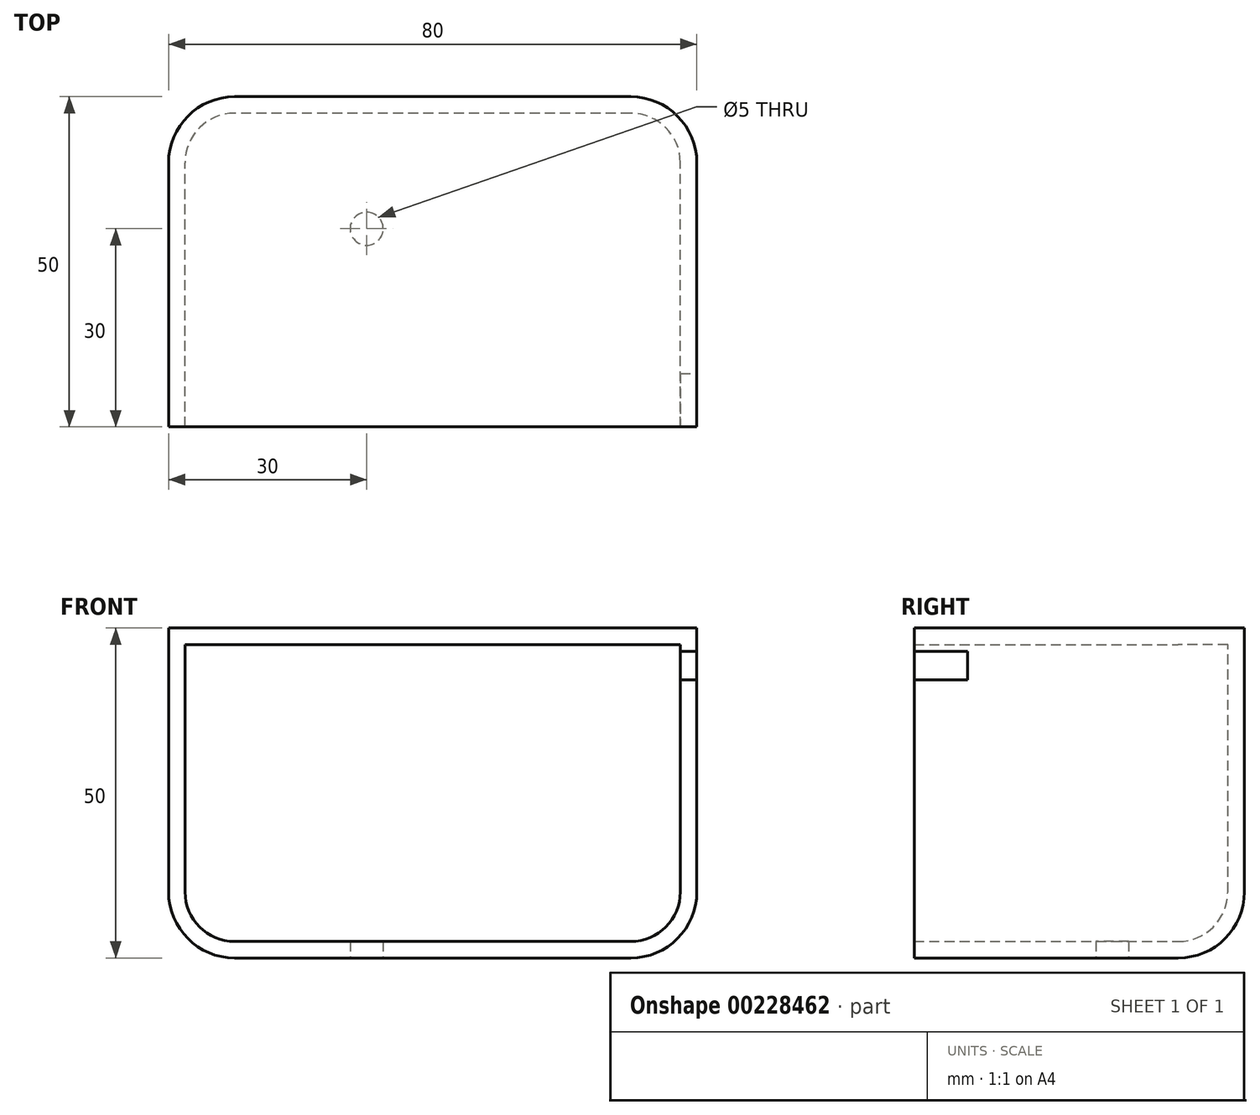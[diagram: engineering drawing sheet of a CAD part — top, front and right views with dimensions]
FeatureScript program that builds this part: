
annotation { "Feature Type Name" : "Feature", "Feature Type Description" : "" }
export const myFeature = defineFeature(function(context is Context, id is Id, definition is map)
    precondition{}
    {
        {
            var Q0;
            Q0=qCreatedBy(makeId("Front.planeOp"),FACE);
            var sketch = newSketch(context, id + "F0", { "sketchPlane" : qUnion([Q0])});
            skLineSegment(sketch, "E0.bottom", {"start": v(40, -25) * mm, "end": v(-40, -25) * mm});
            skLineSegment(sketch, "E0.top", {"start": v(40, 25) * mm, "end": v(-40, 25) * mm});
            skLineSegment(sketch, "E0.left", {"start": v(40, -25) * mm, "end": v(40, 25) * mm});
            skLineSegment(sketch, "E0.right", {"start": v(-40, -25) * mm, "end": v(-40, 25) * mm});
            skPoint(sketch, "E0.middle", {"position": v(0, 0) * mm});
            skSolve(sketch);
        }
        {
            var Q0;
            Q0 = qSketchRegion(id + "F0", true);
            extrude(context, id + "F1", {"entities" : qUnion([Q0]), "depth" : 50 * mm});
        }
        {
            var Q0;
            Q0=makeQuery(id+"F1.opExtrude","SWEPT_EDGE",EDGE,{"disambiguationData":[OSD([sQuery(id+"F0.wireOp",EDGE,"E0.bottom"),sQuery(id+"F0.wireOp",EDGE,"E0.left")])]});
            var Q1;
            Q1=makeQuery(id+"F1.opExtrude","SWEPT_EDGE",EDGE,{"disambiguationData":[OSD([sQuery(id+"F0.wireOp",EDGE,"E0.bottom"),sQuery(id+"F0.wireOp",EDGE,"E0.right")])]});
            var Q2;
            Q2=makeQuery(id+"F1.opExtrude","CAP_EDGE",EDGE,{"disambiguationData":[OSD([sQuery(id+"F0.wireOp",EDGE,"E0.left")])],"isStart":true});
            var Q3;
            Q3=makeQuery(id+"F1.opExtrude","CAP_EDGE",EDGE,{"disambiguationData":[OSD([sQuery(id+"F0.wireOp",EDGE,"E0.bottom")])],"isStart":true});
            var Q4;
            Q4=makeQuery(id+"F1.opExtrude","CAP_EDGE",EDGE,{"disambiguationData":[OSD([sQuery(id+"F0.wireOp",EDGE,"E0.right")])],"isStart":true});
            fillet(context, id + "F2", {"entities" : qUnion([Q0, Q1, Q2, Q3, Q4]), "radius" : 10 * mm, "tangentPropagation" : true, "allowEdgeOverflow" : false});
        }
        {
            var Q0;
            Q0=makeQuery(id+"F1.opExtrude","CAP_FACE",FACE,{"disambiguationData":[OSD([sQuery(id+"F0.wireOp",EDGE,"E0.bottom"),sQuery(id+"F0.wireOp",EDGE,"E0.top"),sQuery(id+"F0.wireOp",EDGE,"E0.left"),sQuery(id+"F0.wireOp",EDGE,"E0.right")])],"isStart":false});
            shell(context, id + "F3", {"entities" : qUnion([Q0]), "thickness" : 2.5 * mm});
        }
        {
            var Q0;
            Q0=makeQuery(id+"F1.opExtrude","SWEPT_FACE",FACE,{"disambiguationData":[OSD([sQuery(id+"F0.wireOp",EDGE,"E0.bottom")])]});
            var sketch = newSketch(context, id + "F4", { "sketchPlane" : qUnion([Q0])});
            skPoint(sketch, "E1", {"position": v(-10, 20) * mm});
            skSolve(sketch);
        }
        {
            var Q0;
            Q0=sQuery(id+"F4.wireOp",VERTEX,"E1");
            var Q1;
            Q1=makeQuery(id+"F1.opExtrude","SWEPT_BODY",BODY,{"disambiguationData":[OSD([sQuery(id+"F0.wireOp",EDGE,"E0.bottom"),sQuery(id+"F0.wireOp",EDGE,"E0.top"),sQuery(id+"F0.wireOp",EDGE,"E0.left"),sQuery(id+"F0.wireOp",EDGE,"E0.right")])]});
            hole(context, id + "F5", {"style" : HoleStyle.SIMPLE, "endStyle" : HoleEndStyle.BLIND, "holeDiameter" : 5 * mm, "holeDepth" : 12 * mm, "locations" : qUnion([Q0]), "scope" : qUnion([Q1])});
        }
        {
            var Q0;
            Q0=makeQuery(id+"F1.opExtrude","SWEPT_FACE",FACE,{"disambiguationData":[OSD([sQuery(id+"F0.wireOp",EDGE,"E0.left")])]});
            var sketch = newSketch(context, id + "F6", { "sketchPlane" : qUnion([Q0])});
            skLineSegment(sketch, "E2.bottom", {"start": v(-50, 21.43) * mm, "end": v(-41.91, 21.43) * mm});
            skLineSegment(sketch, "E2.top", {"start": v(-50, 17.12) * mm, "end": v(-41.91, 17.12) * mm});
            skLineSegment(sketch, "E2.left", {"start": v(-50, 21.43) * mm, "end": v(-50, 17.12) * mm});
            skLineSegment(sketch, "E2.right", {"start": v(-41.91, 21.43) * mm, "end": v(-41.91, 17.12) * mm});
            skSolve(sketch);
        }
        {
            var Q0;
            Q0 = qSketchRegion(id + "F6", true);
            extrude(context, id + "F7", {"entities" : qUnion([Q0]), "operationType" : NewBodyOperationType.REMOVE, "oppositeDirection" : true, "depth" : 25 * mm});
        }
    });
